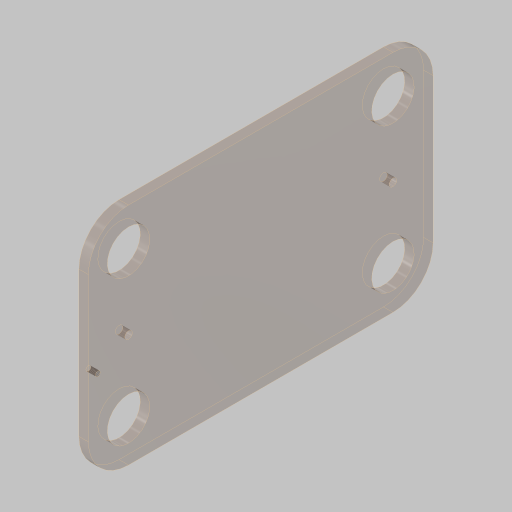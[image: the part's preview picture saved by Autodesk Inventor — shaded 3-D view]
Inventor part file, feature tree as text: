
AUTODESK INVENTOR PART (.ipt)
format: ipt  version: 2023.5 (Build 275446000, 446)  size: 151,040 bytes
history: native  units: in
note: dims shown in document units (in); Inventor stores cm internally (conversion verified against a paired STEP export)
features: sketch x2, hole x2, extrude x1
ambient origin geometry x8: Origin, YZ Plane, XZ Plane, XY Plane, X Axis, Y Axis, Z Axis, Center Point
bodies: Solid1 (feature_tree)
feature tree (5):
  sketch  "Sketch1"  dims[d0=1.125in d2=12.0in]
  extrude  "Extrusion1"  Depth=12.0in
  hole  "Hole1"  [1 undecoded]
  hole  "Hole2"  [1 undecoded]
  sketch  "Sketch3"  dims[d3=4.5in d4=3.0in d6=0.25in d7=0.5in d8=3.8356in d9=0.25in d10=0.0in d11=0.201in d12=0.38in d13=0.385in d14=0.25in d15=0.5635in d16=1.0in d17=0.8108in d18=0.25in d29=0.25in d30=2.5in d31=0.13in d32=0.328in d33=0.375in d34=0.25in d35=0.5635in d36=0.25in d37=0.8108in]
note: 2 required parameter values undecoded (feature->parameter linkage not recoverable at this tier; creation-order binding heuristic only, values carry confidence <= 0.55)
